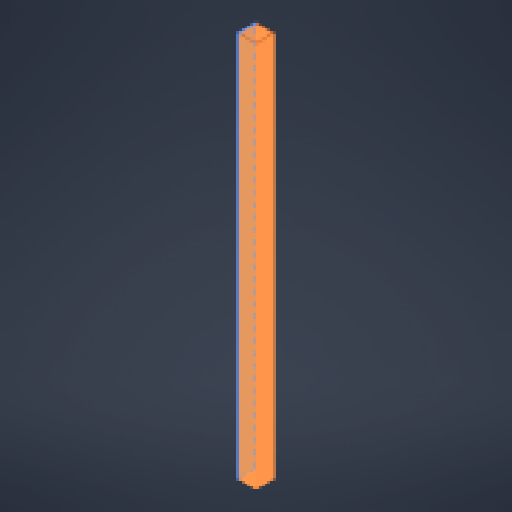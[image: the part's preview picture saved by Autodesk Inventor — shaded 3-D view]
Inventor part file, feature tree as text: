
AUTODESK INVENTOR PART (.ipt)
format: ipt  version: 2024 (Build 280153000, 153)  size: 139,776 bytes
history: native  units: mm
features: other x2, extrude x1, sketch x1
ambient origin geometry x8: Origin, YZ Plane, XZ Plane, XY Plane, X Axis, Y Axis, Z Axis, Center Point
bodies: Body1 (feature_tree)
feature tree (4):
  other  "Твердое тело1"
  other  "РабПлоскость2"
  extrude  "Выдавливание1"  Depth=20.0mm
  sketch  "Эскиз1"
